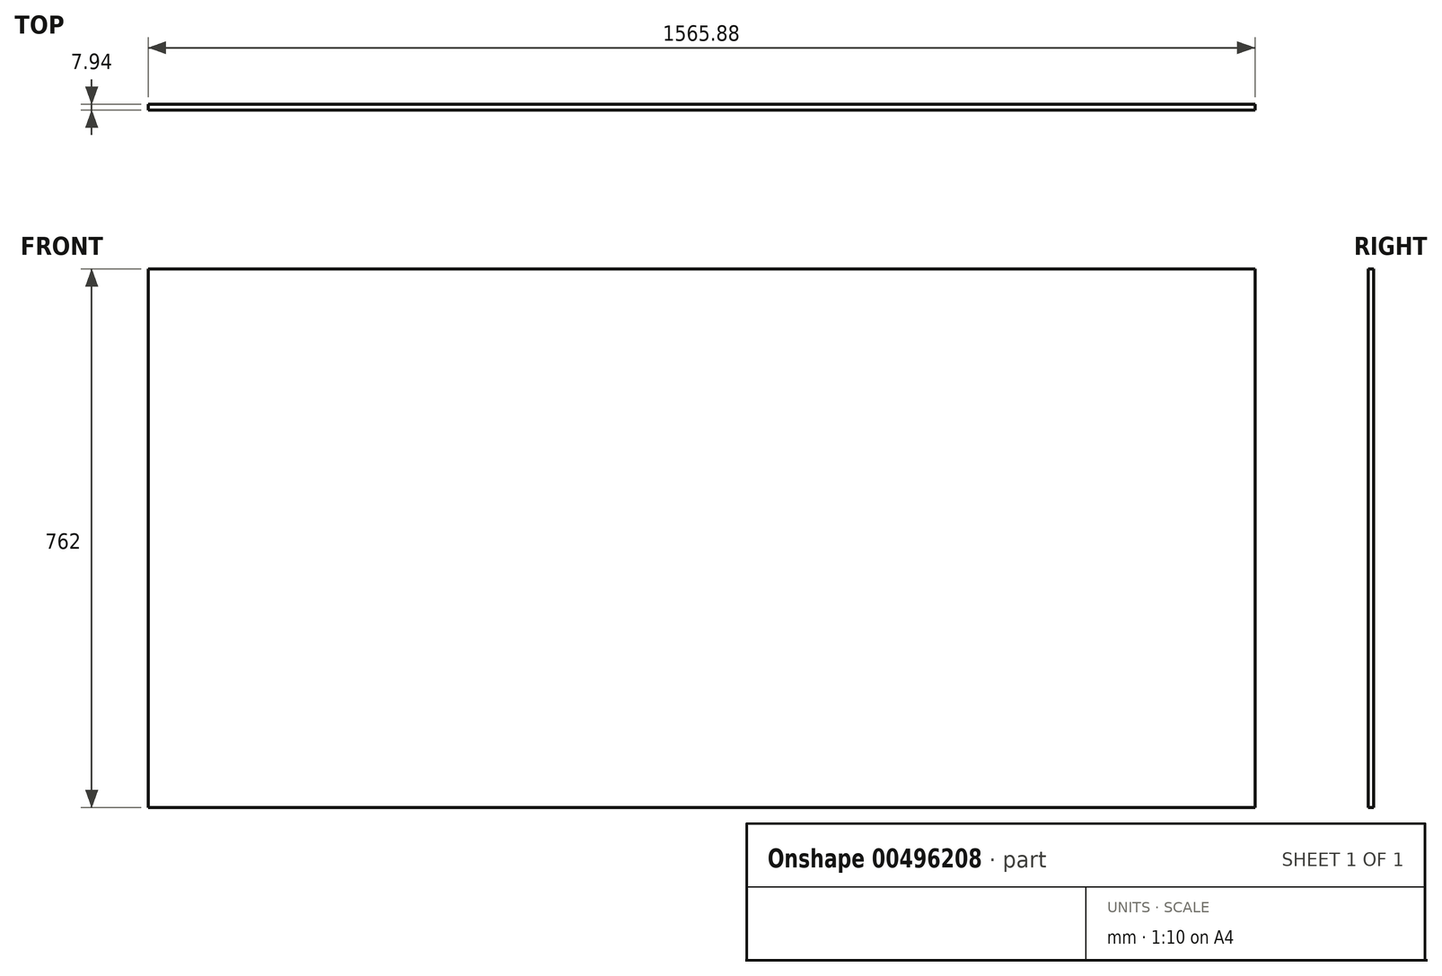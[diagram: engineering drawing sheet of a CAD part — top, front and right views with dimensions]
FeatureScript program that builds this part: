
annotation { "Feature Type Name" : "Feature", "Feature Type Description" : "" }
export const myFeature = defineFeature(function(context is Context, id is Id, definition is map)
    precondition{}
    {
        {
            var Q0;
            Q0=qCreatedBy(makeId("Front.planeOp"),FACE);
            var sketch = newSketch(context, id + "F0", { "sketchPlane" : qUnion([Q0])});
            skLineSegment(sketch, "E0.bottom", {"start": v(-782.94, 762) * mm, "end": v(782.94, 762) * mm});
            skLineSegment(sketch, "E0.top", {"start": v(-782.94, 0) * mm, "end": v(782.94, 0) * mm});
            skLineSegment(sketch, "E0.left", {"start": v(-782.94, 762) * mm, "end": v(-782.94, 0) * mm});
            skLineSegment(sketch, "E0.right", {"start": v(782.94, 762) * mm, "end": v(782.94, 0) * mm});
            skSolve(sketch);
        }
        {
            var Q0;
            Q0 = qSketchRegion(id + "F0", true);
            extrude(context, id + "F1", {"entities" : qUnion([Q0]), "depth" : 7.94 * mm, "offsetDistance" : 25.4 * mm});
        }
    });
